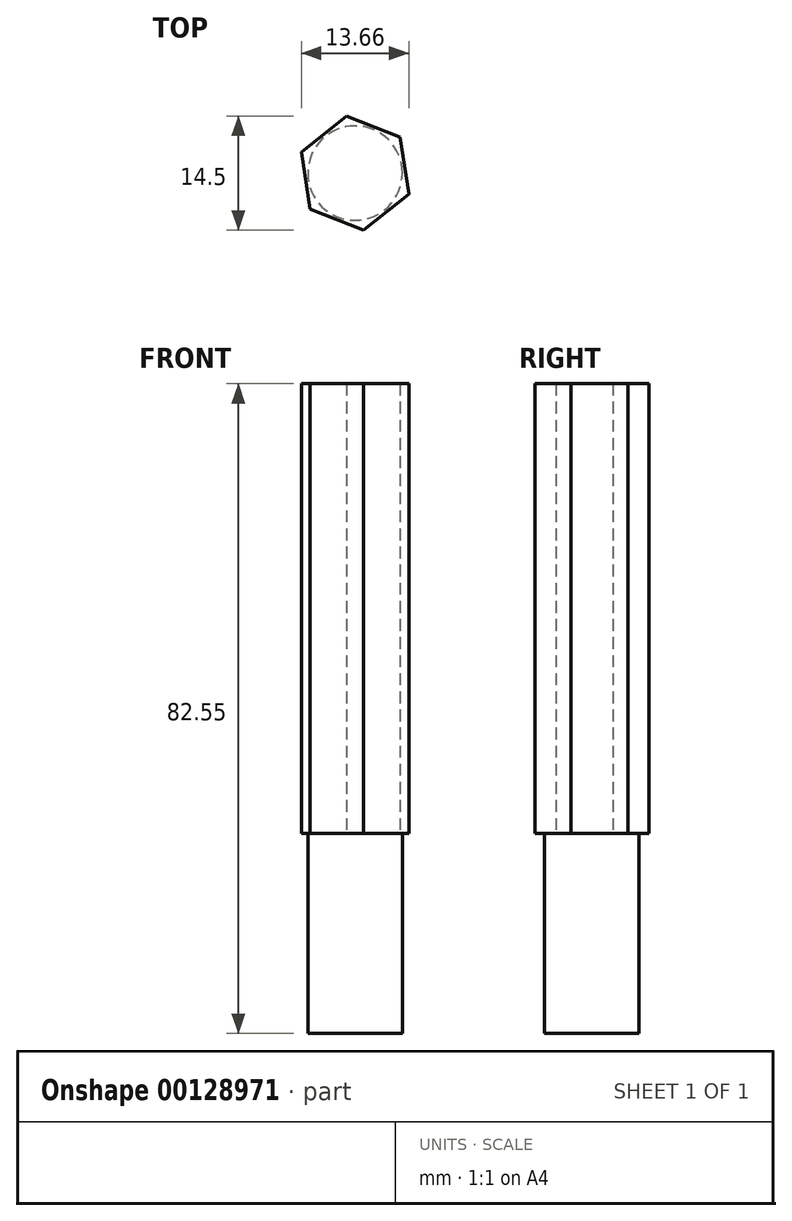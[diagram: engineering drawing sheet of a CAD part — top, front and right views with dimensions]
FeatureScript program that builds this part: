
annotation { "Feature Type Name" : "Feature", "Feature Type Description" : "" }
export const myFeature = defineFeature(function(context is Context, id is Id, definition is map)
    precondition{}
    {
        {
            var Q0;
            Q0=qCreatedBy(makeId("Top.planeOp"),FACE);
            var sketch = newSketch(context, id + "F0", { "sketchPlane" : qUnion([Q0])});
            skCircle(sketch, "E0.cCircle", {"center": v(0, 0) * mm, "radius": 6.35 * mm, "construction": true});
            skLineSegment(sketch, "E0.0", {"start": v(6.83, -2.67) * mm, "end": v(1.1, -7.25) * mm});
            skLineSegment(sketch, "E0.1", {"start": v(1.1, -7.25) * mm, "end": v(-5.73, -4.58) * mm});
            skLineSegment(sketch, "E0.2", {"start": v(-5.73, -4.58) * mm, "end": v(-6.83, 2.67) * mm});
            skLineSegment(sketch, "E0.3", {"start": v(-6.83, 2.67) * mm, "end": v(-1.1, 7.25) * mm});
            skLineSegment(sketch, "E0.4", {"start": v(-1.1, 7.25) * mm, "end": v(5.73, 4.58) * mm});
            skLineSegment(sketch, "E0.5", {"start": v(5.73, 4.58) * mm, "end": v(6.83, -2.67) * mm});
            skPoint(sketch, "E0.0.midPoint", {"position": v(3.97, -4.96) * mm});
            skSolve(sketch);
        }
        {
            var Q0;
            Q0 = qSketchRegion(id + "F0", true);
            extrude(context, id + "F1", {"entities" : qUnion([Q0]), "depth" : 57.15 * mm});
        }
        {
            var Q0;
            Q0=qCreatedBy(makeId("Top.planeOp"),FACE);
            var sketch = newSketch(context, id + "F2", { "sketchPlane" : qUnion([Q0])});
            skCircle(sketch, "E1", {"center": v(0, 0) * mm, "radius": 6 * mm});
            skSolve(sketch);
        }
        {
            var Q0;
            Q0 = qSketchRegion(id + "F2", true);
            extrude(context, id + "F3", {"entities" : qUnion([Q0]), "operationType" : NewBodyOperationType.ADD, "oppositeDirection" : true, "depth" : 25.4 * mm});
        }
    });
